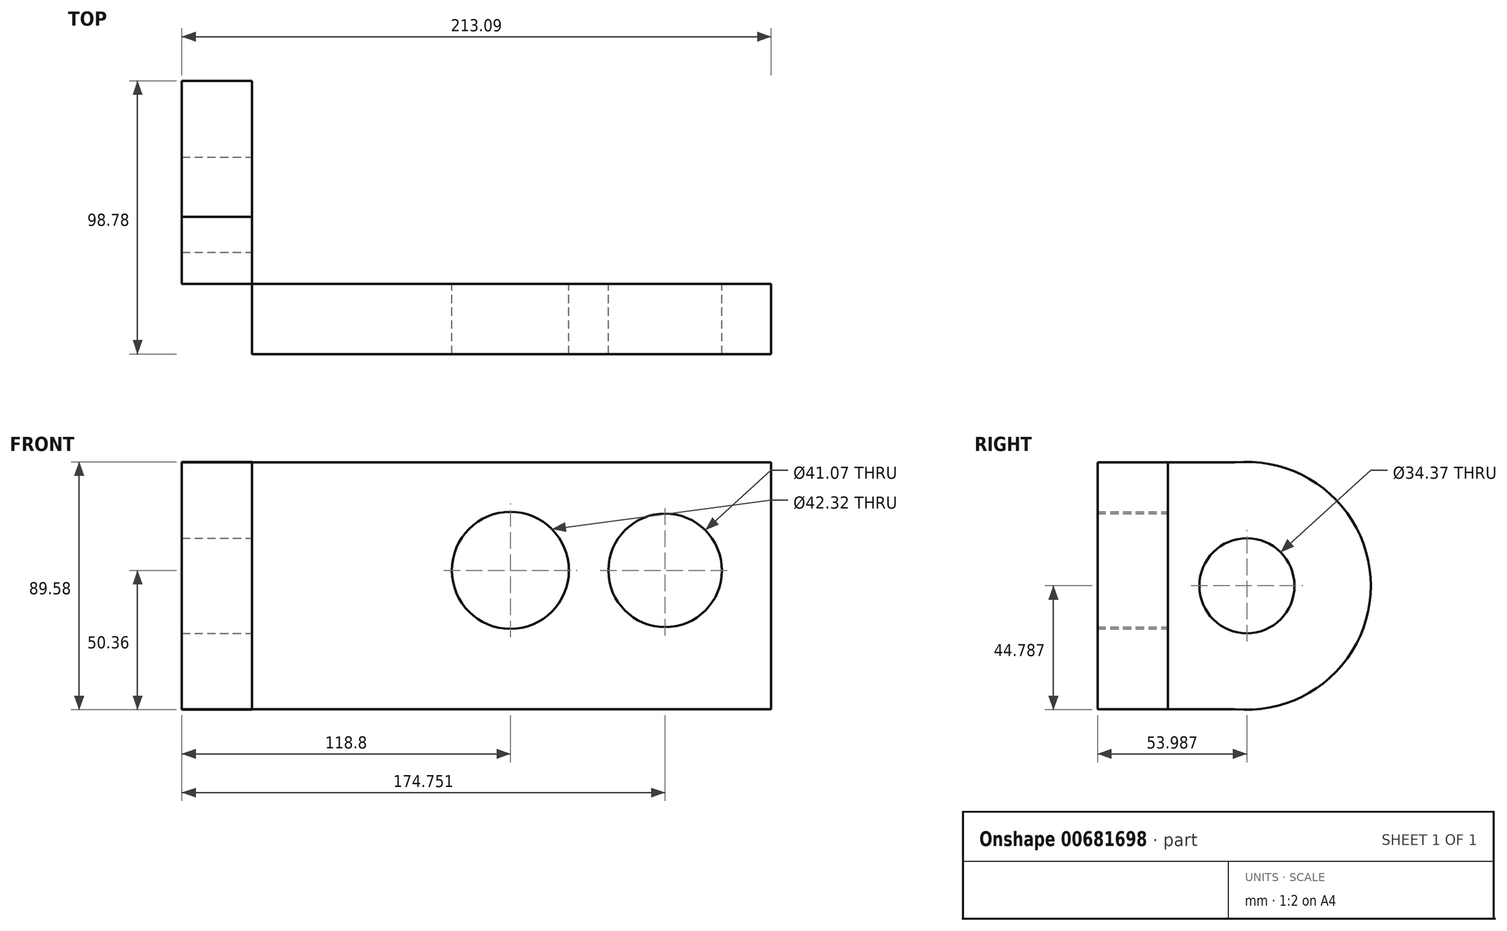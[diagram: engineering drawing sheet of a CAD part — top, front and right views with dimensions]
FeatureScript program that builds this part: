
annotation { "Feature Type Name" : "Feature", "Feature Type Description" : "" }
export const myFeature = defineFeature(function(context is Context, id is Id, definition is map)
    precondition{}
    {
        {
            var Q0;
            Q0=qCreatedBy(makeId("Front.planeOp"),FACE);
            var sketch = newSketch(context, id + "F0", { "sketchPlane" : qUnion([Q0])});
            skLineSegment(sketch, "E0.bottom", {"start": v(-93.4, 39) * mm, "end": v(94.3, 39) * mm});
            skLineSegment(sketch, "E0.top", {"start": v(-93.4, -50.15) * mm, "end": v(94.3, -50.15) * mm});
            skLineSegment(sketch, "E0.left", {"start": v(-93.4, 39) * mm, "end": v(-93.4, -50.15) * mm});
            skLineSegment(sketch, "E0.right", {"start": v(94.3, 39) * mm, "end": v(94.3, -50.15) * mm});
            skCircle(sketch, "E1", {"center": v(55.95, 0) * mm, "radius": 20.53 * mm});
            skCircle(sketch, "E2", {"center": v(0, 0) * mm, "radius": 21.16 * mm});
            skSolve(sketch);
        }
        {
            var Q0;
            Q0 = qSketchRegion(id + "F0", true);
            extrude(context, id + "F1", {"entities" : qUnion([Q0]), "depth" : 25.4 * mm, "offsetDistance" : 25.4 * mm});
        }
        {
            var Q0;
            Q0=makeQuery(id+"F1.opExtrude","SWEPT_FACE",FACE,{"disambiguationData":[OSD([sQuery(id+"F0.wireOp",EDGE,"E0.left")])]});
            var sketch = newSketch(context, id + "F2", { "sketchPlane" : qUnion([Q0])});
            skLineSegment(sketch, "E3", {"start": v(0, 39) * mm, "end": v(-24.27, 39) * mm});
            skLineSegment(sketch, "E4", {"start": v(0, -50.15) * mm, "end": v(-24.27, -50.15) * mm});
            skArc(sketch, "E5", {"start": v(-24.27, 39) * mm, "mid": v(-73.38, -5.57) * mm, "end": v(-24.27, -50.15) * mm});
            skCircle(sketch, "E6", {"center": v(-28.59, -5.57) * mm, "radius": 17.19 * mm});
            skSolve(sketch);
        }
        {
            var Q0;
            Q0=makeQuery(id+"F2.imprint","IMPRINT",FACE,{"disambiguationData":[TD([[makeQuery(id+"F2.imprint","IMPRINT",EDGE,{"derivedFrom":sQuery(id+"F2.wireOp",EDGE,"E3")}),1.0]])]});
            extrude(context, id + "F3", {"entities" : qUnion([Q0]), "depth" : 25.4 * mm, "offsetDistance" : 25.4 * mm});
        }
    });
